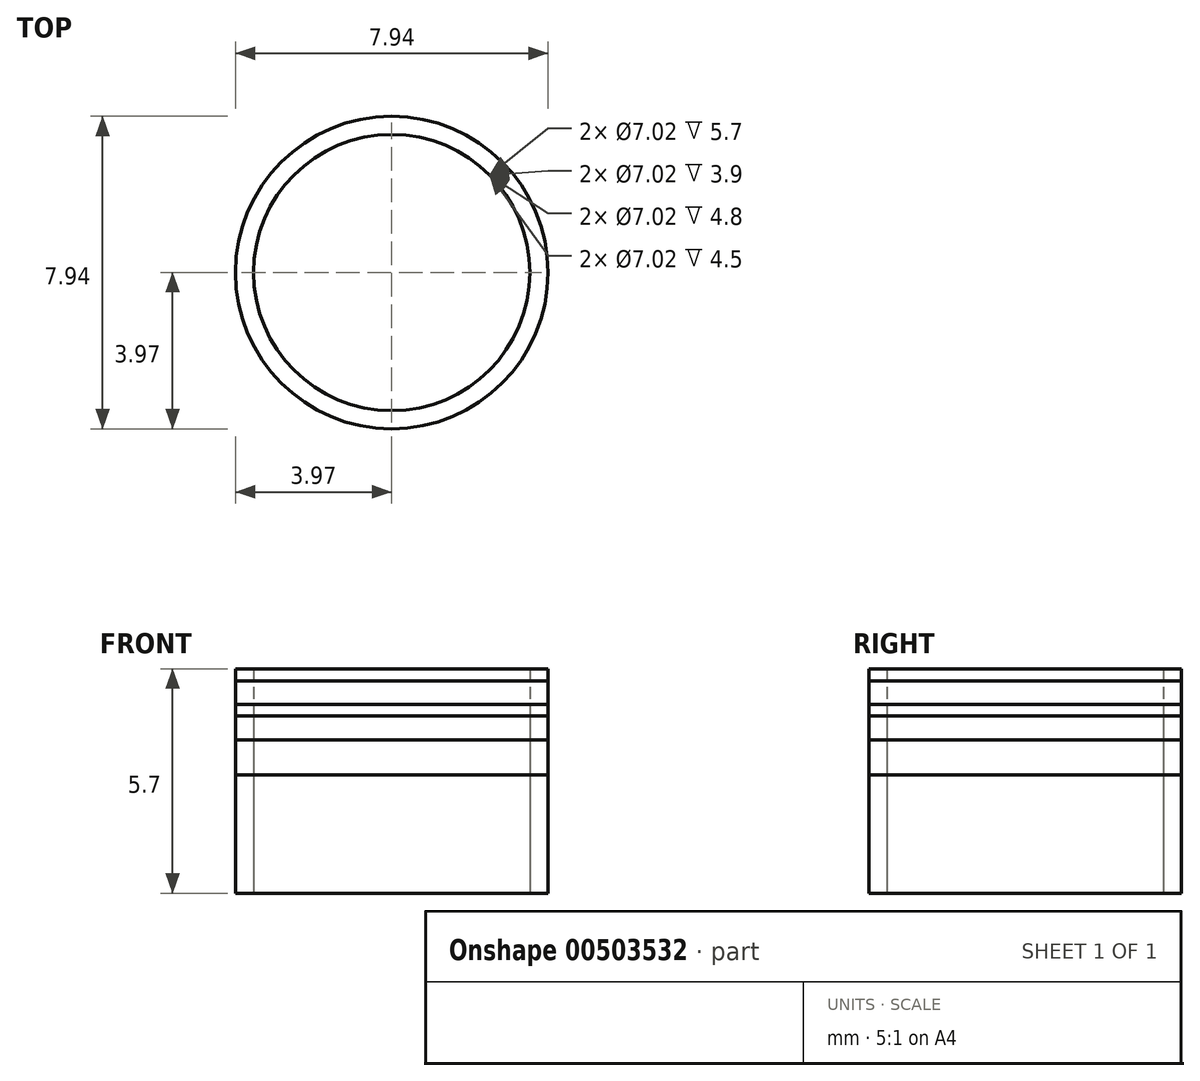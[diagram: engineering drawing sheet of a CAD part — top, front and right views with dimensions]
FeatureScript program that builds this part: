
annotation { "Feature Type Name" : "Feature", "Feature Type Description" : "" }
export const myFeature = defineFeature(function(context is Context, id is Id, definition is map)
    precondition{}
    {
        {
            var Q0;
            Q0=qCreatedBy(makeId("Top.planeOp"),FACE);
            var sketch = newSketch(context, id + "F0", { "sketchPlane" : qUnion([Q0])});
            skCircle(sketch, "E0", {"center": v(0, 0) * mm, "radius": 1.32 * mm});
            skCircle(sketch, "E1", {"center": v(0, 0) * mm, "radius": 1.17 * mm});
            skSolve(sketch);
        }
        {
            var Q0;
            Q0=makeQuery(id+"F0.imprint","IMPRINT",FACE,{"disambiguationData":[TD([[makeQuery(id+"F0.imprint","IMPRINT",EDGE,{"derivedFrom":sQuery(id+"F0.wireOp",EDGE,"E0")}),1.0]])]});
            extrude(context, id + "F1", {"entities" : qUnion([Q0]), "depth" : 1.5 * mm});
        }
        {
            var Q0;
            Q0=makeQuery(id+"F0.imprint","IMPRINT",FACE,{"disambiguationData":[TD([[makeQuery(id+"F0.imprint","IMPRINT",EDGE,{"derivedFrom":sQuery(id+"F0.wireOp",EDGE,"E0")}),1.0]])]});
            extrude(context, id + "F2", {"entities" : qUnion([Q0]), "depth" : 1.6 * mm});
        }
        {
            var Q0;
            Q0=makeQuery(id+"F0.imprint","IMPRINT",FACE,{"disambiguationData":[TD([[makeQuery(id+"F0.imprint","IMPRINT",EDGE,{"derivedFrom":sQuery(id+"F0.wireOp",EDGE,"E0")}),1.0]])]});
            var Q1;
            Q1=makeQuery(id+"F0.imprint","IMPRINT",FACE,{"disambiguationData":[TD([[makeQuery(id+"F0.imprint","IMPRINT",EDGE,{"derivedFrom":sQuery(id+"F0.wireOp",EDGE,"E1")}),1.0]])]});
            extrude(context, id + "F3", {"entities" : qUnion([Q0, Q1]), "depth" : 1.8 * mm});
        }
        {
            var Q0;
            Q0=makeQuery(id+"F0.imprint","IMPRINT",FACE,{"disambiguationData":[TD([[makeQuery(id+"F0.imprint","IMPRINT",EDGE,{"derivedFrom":sQuery(id+"F0.wireOp",EDGE,"E0")}),1.0]])]});
            extrude(context, id + "F4", {"entities" : qUnion([Q0]), "depth" : 1.9 * mm});
        }
        {
            var Q0;
            Q0=makeQuery(id+"F0.imprint","IMPRINT",FACE,{"disambiguationData":[TD([[makeQuery(id+"F0.imprint","IMPRINT",EDGE,{"derivedFrom":sQuery(id+"F0.wireOp",EDGE,"E0")}),1.0]])]});
            extrude(context, id + "F5", {"entities" : qUnion([Q0]), "depth" : 1.3 * mm});
        }
        {
            var Q0;
            Q0=makeQuery(id+"F0.imprint","IMPRINT",FACE,{"disambiguationData":[TD([[makeQuery(id+"F0.imprint","IMPRINT",EDGE,{"derivedFrom":sQuery(id+"F0.wireOp",EDGE,"E0")}),1.0]])]});
            var Q1;
            Q1=makeQuery(id+"F0.imprint","IMPRINT",FACE,{"disambiguationData":[TD([[makeQuery(id+"F0.imprint","IMPRINT",EDGE,{"derivedFrom":sQuery(id+"F0.wireOp",EDGE,"E1")}),1.0]])]});
            extrude(context, id + "F6", {"entities" : qUnion([Q0, Q1]), "depth" : 1 * mm});
        }
        {
            var Q0;
            Q0=makeQuery(id+"F1.opExtrude","SWEPT_BODY",BODY,{"disambiguationData":[OSD([sQuery(id+"F0.wireOp",EDGE,"E0"),sQuery(id+"F0.wireOp",EDGE,"E1")])]});
            var Q1;
            Q1=makeQuery(id+"F2.opExtrude","SWEPT_BODY",BODY,{"disambiguationData":[OSD([sQuery(id+"F0.wireOp",EDGE,"E0"),sQuery(id+"F0.wireOp",EDGE,"E1")])]});
            var Q2;
            Q2=makeQuery(id+"F3.opExtrude","SWEPT_BODY",BODY,{"disambiguationData":[OSD([sQuery(id+"F0.wireOp",EDGE,"E0"),sQuery(id+"F0.wireOp",EDGE,"E1")])]});
            var Q3;
            Q3=makeQuery(id+"F4.opExtrude","SWEPT_BODY",BODY,{"disambiguationData":[OSD([sQuery(id+"F0.wireOp",EDGE,"E0"),sQuery(id+"F0.wireOp",EDGE,"E1")])]});
            var Q4;
            Q4=makeQuery(id+"F5.opExtrude","SWEPT_BODY",BODY,{"disambiguationData":[OSD([sQuery(id+"F0.wireOp",EDGE,"E0"),sQuery(id+"F0.wireOp",EDGE,"E1")])]});
            var Q5;
            Q5=makeQuery(id+"F6.opExtrude","SWEPT_BODY",BODY,{"disambiguationData":[OSD([sQuery(id+"F0.wireOp",EDGE,"E0"),sQuery(id+"F0.wireOp",EDGE,"E1")])]});
            var Q6;
            Q6=qCreatedBy(makeId("Origin.pointOp"),VERTEX);
            transform(context, id + "F7", {"entities" : qUnion([Q0, Q1, Q2, Q3, Q4, Q5]), "transformType" : TransformType.SCALE_UNIFORMLY, "scale" : 3, "makeCopy" : false, "scalePoint" : qUnion([Q6])});
        }
    });
